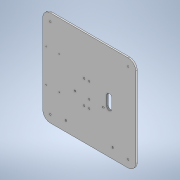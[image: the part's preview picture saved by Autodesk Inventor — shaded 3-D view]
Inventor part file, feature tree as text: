
AUTODESK INVENTOR PART (.ipt)
format: ipt  version: 2020 (Build 240168000, 168)  size: 171,008 bytes
history: native  units: in
note: dims shown in document units (in); Inventor stores cm internally (conversion verified against a paired STEP export)
features: fillet x2, extrude x1, sketch x1
ambient origin geometry x8: Origin, YZ Plane, XZ Plane, XY Plane, X Axis, Y Axis, Z Axis, Center Point
bodies: Body1 (feature_tree)
feature tree (4):
  extrude  "Extrusion2"  Depth=0.5906in
  fillet  "Fillet3"  Radius=0.1969in
  fillet  "Fillet4"  [1 undecoded]
  sketch  "Sketch1"  dims[d4=0.1181in d5=0.0in d6=0.5906in d7=0.1969in]
note: 1 required parameter value undecoded (feature->parameter linkage not recoverable at this tier; creation-order binding heuristic only, values carry confidence <= 0.55)
